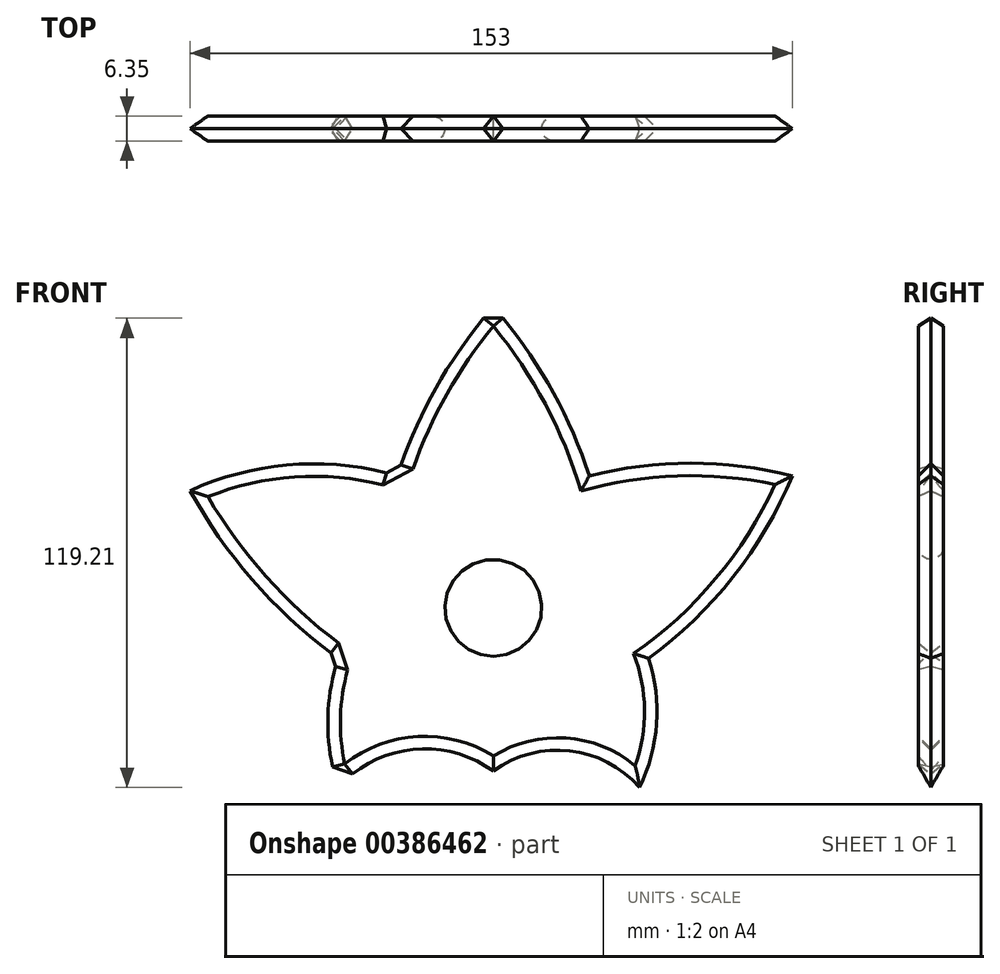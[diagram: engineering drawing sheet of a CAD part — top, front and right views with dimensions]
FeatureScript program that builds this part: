
annotation { "Feature Type Name" : "Feature", "Feature Type Description" : "" }
export const myFeature = defineFeature(function(context is Context, id is Id, definition is map)
    precondition{}
    {
        {
            var Q0;
            Q0=qCreatedBy(makeId("Front.planeOp"),FACE);
            var sketch = newSketch(context, id + "F0", { "sketchPlane" : qUnion([Q0])});
            skCircle(sketch, "E0.cCircle", {"center": v(0, 0) * mm, "radius": 41.47 * mm, "construction": true});
            skLineSegment(sketch, "E0.0", {"start": v(0, -41.47) * mm, "end": v(-39.44, -12.81) * mm});
            skLineSegment(sketch, "E0.1", {"start": v(-39.44, -12.81) * mm, "end": v(-24.37, 33.55) * mm});
            skLineSegment(sketch, "E0.2", {"start": v(-24.37, 33.55) * mm, "end": v(24.37, 33.55) * mm});
            skLineSegment(sketch, "E0.3", {"start": v(24.37, 33.55) * mm, "end": v(39.44, -12.81) * mm});
            skLineSegment(sketch, "E0.4", {"start": v(39.44, -12.81) * mm, "end": v(0, -41.47) * mm});
            skCircle(sketch, "E1", {"center": v(0, 0) * mm, "radius": 12.32 * mm});
            skArc(sketch, "E2", {"start": v(0, 76.5) * mm, "mid": v(-14.36, 56.26) * mm, "end": v(-24.37, 33.55) * mm});
            skArc(sketch, "E3", {"start": v(24.37, 33.55) * mm, "mid": v(14.36, 56.26) * mm, "end": v(0, 76.5) * mm});
            skArc(sketch, "E4", {"start": v(-77.03, 29.76) * mm, "mid": v(-60.58, 6.4) * mm, "end": v(-39.44, -12.81) * mm});
            skArc(sketch, "E5", {"start": v(-24.37, 33.55) * mm, "mid": v(-51.04, 36.4) * mm, "end": v(-77.03, 29.76) * mm});
            skArc(sketch, "E6", {"start": v(75.97, 33.55) * mm, "mid": v(50.17, 36.75) * mm, "end": v(24.37, 33.55) * mm});
            skArc(sketch, "E7", {"start": v(39.44, -12.81) * mm, "mid": v(60.91, 7.84) * mm, "end": v(75.97, 33.55) * mm});
            skArc(sketch, "E8", {"start": v(-39.44, -12.81) * mm, "mid": v(-42.03, -29.21) * mm, "end": v(-39.44, -45.61) * mm});
            skArc(sketch, "E9", {"start": v(0, -41.47) * mm, "mid": v(-20.51, -35.97) * mm, "end": v(-39.44, -45.61) * mm});
            skArc(sketch, "E10", {"start": v(37.16, -45.61) * mm, "mid": v(19.38, -36.34) * mm, "end": v(0, -41.47) * mm});
            skArc(sketch, "E11", {"start": v(37.16, -45.61) * mm, "mid": v(41.48, -29.43) * mm, "end": v(39.44, -12.81) * mm});
            skSolve(sketch);
        }
        {
            var Q0;
            Q0=makeQuery(id+"F0.imprint","IMPRINT",FACE,{"disambiguationData":[TD([[makeQuery(id+"F0.imprint","IMPRINT",EDGE,{"derivedFrom":sQuery(id+"F0.wireOp",EDGE,"E0.0")}),-1.0]])]});
            var Q1;
            Q1=makeQuery(id+"F0.imprint","IMPRINT",FACE,{"disambiguationData":[TD([[makeQuery(id+"F0.imprint","IMPRINT",EDGE,{"derivedFrom":sQuery(id+"F0.wireOp",EDGE,"E0.1")}),1.0]])]});
            var Q2;
            Q2=makeQuery(id+"F0.imprint","IMPRINT",FACE,{"disambiguationData":[TD([[makeQuery(id+"F0.imprint","IMPRINT",EDGE,{"derivedFrom":sQuery(id+"F0.wireOp",EDGE,"E0.2")}),1.0]])]});
            var Q3;
            Q3=makeQuery(id+"F0.imprint","IMPRINT",FACE,{"disambiguationData":[TD([[makeQuery(id+"F0.imprint","IMPRINT",EDGE,{"derivedFrom":sQuery(id+"F0.wireOp",EDGE,"E0.3")}),1.0]])]});
            var Q4;
            Q4=makeQuery(id+"F0.imprint","IMPRINT",FACE,{"disambiguationData":[TD([[makeQuery(id+"F0.imprint","IMPRINT",EDGE,{"derivedFrom":sQuery(id+"F0.wireOp",EDGE,"E0.4")}),1.0]])]});
            var Q5;
            Q5=makeQuery(id+"F0.imprint","IMPRINT",FACE,{"disambiguationData":[TD([[makeQuery(id+"F0.imprint","IMPRINT",EDGE,{"derivedFrom":sQuery(id+"F0.wireOp",EDGE,"E0.0")}),1.0]])]});
            extrude(context, id + "F1", {"entities" : qUnion([Q0, Q1, Q2, Q3, Q4, Q5]), "depth" : 6.35 * mm});
        }
        {
            var Q0;
            Q0=makeQuery(id+"F1.opExtrude","CAP_EDGE",EDGE,{"disambiguationData":[OSD([sQuery(id+"F0.wireOp",EDGE,"E4")])],"isStart":true});
            var Q1;
            Q1=makeQuery(id+"F1.opExtrude","CAP_EDGE",EDGE,{"disambiguationData":[OSD([sQuery(id+"F0.wireOp",EDGE,"E4")])],"isStart":false});
            var Q2;
            Q2=makeQuery(id+"F1.opExtrude","CAP_EDGE",EDGE,{"disambiguationData":[OSD([sQuery(id+"F0.wireOp",EDGE,"E2")])],"isStart":false});
            var Q3;
            Q3=makeQuery(id+"F1.opExtrude","SWEPT_FACE",FACE,{"disambiguationData":[OSD([sQuery(id+"F0.wireOp",EDGE,"E2")])]});
            var Q4;
            Q4=makeQuery(id+"F1.opExtrude","SWEPT_FACE",FACE,{"disambiguationData":[OSD([sQuery(id+"F0.wireOp",EDGE,"E8")])]});
            var Q5;
            Q5=makeQuery(id+"F1.opExtrude","CAP_EDGE",EDGE,{"disambiguationData":[OSD([sQuery(id+"F0.wireOp",EDGE,"E3")])],"isStart":true});
            var Q6;
            Q6=makeQuery(id+"F1.opExtrude","CAP_EDGE",EDGE,{"disambiguationData":[OSD([sQuery(id+"F0.wireOp",EDGE,"E6")])],"isStart":true});
            var Q7;
            Q7=makeQuery(id+"F1.opExtrude","CAP_EDGE",EDGE,{"disambiguationData":[OSD([sQuery(id+"F0.wireOp",EDGE,"E7")])],"isStart":true});
            var Q8;
            Q8=makeQuery(id+"F1.opExtrude","CAP_EDGE",EDGE,{"disambiguationData":[OSD([sQuery(id+"F0.wireOp",EDGE,"E11")])],"isStart":true});
            var Q9;
            Q9=makeQuery(id+"F1.opExtrude","CAP_EDGE",EDGE,{"disambiguationData":[OSD([sQuery(id+"F0.wireOp",EDGE,"E5")])],"isStart":false});
            var Q10;
            Q10=makeQuery(id+"F1.opExtrude","CAP_EDGE",EDGE,{"disambiguationData":[OSD([sQuery(id+"F0.wireOp",EDGE,"E3")])],"isStart":false});
            var Q11;
            Q11=makeQuery(id+"F1.opExtrude","CAP_EDGE",EDGE,{"disambiguationData":[OSD([sQuery(id+"F0.wireOp",EDGE,"E6")])],"isStart":false});
            var Q12;
            Q12=makeQuery(id+"F1.opExtrude","CAP_EDGE",EDGE,{"disambiguationData":[OSD([sQuery(id+"F0.wireOp",EDGE,"E7")])],"isStart":false});
            var Q13;
            Q13=makeQuery(id+"F1.opExtrude","CAP_EDGE",EDGE,{"disambiguationData":[OSD([sQuery(id+"F0.wireOp",EDGE,"E11")])],"isStart":false});
            var Q14;
            Q14=makeQuery(id+"F1.opExtrude","CAP_EDGE",EDGE,{"disambiguationData":[OSD([sQuery(id+"F0.wireOp",EDGE,"E9")])],"isStart":false});
            var Q15;
            Q15=makeQuery(id+"F1.opExtrude","CAP_EDGE",EDGE,{"disambiguationData":[OSD([sQuery(id+"F0.wireOp",EDGE,"E9")])],"isStart":true});
            var Q16;
            Q16=makeQuery(id+"F1.opExtrude","CAP_EDGE",EDGE,{"disambiguationData":[OSD([sQuery(id+"F0.wireOp",EDGE,"E10")])],"isStart":true});
            var Q17;
            Q17=makeQuery(id+"F1.opExtrude","CAP_EDGE",EDGE,{"disambiguationData":[OSD([sQuery(id+"F0.wireOp",EDGE,"E10")])],"isStart":false});
            chamfer(context, id + "F2", {"entities" : qUnion([Q0, Q1, Q2, Q3, Q4, Q5, Q6, Q7, Q8, Q9, Q10, Q11, Q12, Q13, Q14, Q15, Q16, Q17]), "width" : 3.17 * mm, "tangentPropagation" : true});
        }
        {
            var Q0;
            Q0=makeQuery(id+"F1.opExtrude","CAP_EDGE",EDGE,{"disambiguationData":[OSD([sQuery(id+"F0.wireOp",EDGE,"E1")])],"isStart":false});
            var Q1;
            Q1=makeQuery(id+"F1.opExtrude","CAP_EDGE",EDGE,{"disambiguationData":[OSD([sQuery(id+"F0.wireOp",EDGE,"E1")])],"isStart":true});
            fillet(context, id + "F3", {"entities" : qUnion([Q0, Q1]), "radius" : 3.17 * mm, "tangentPropagation" : true, "allowEdgeOverflow" : false});
        }
    });
